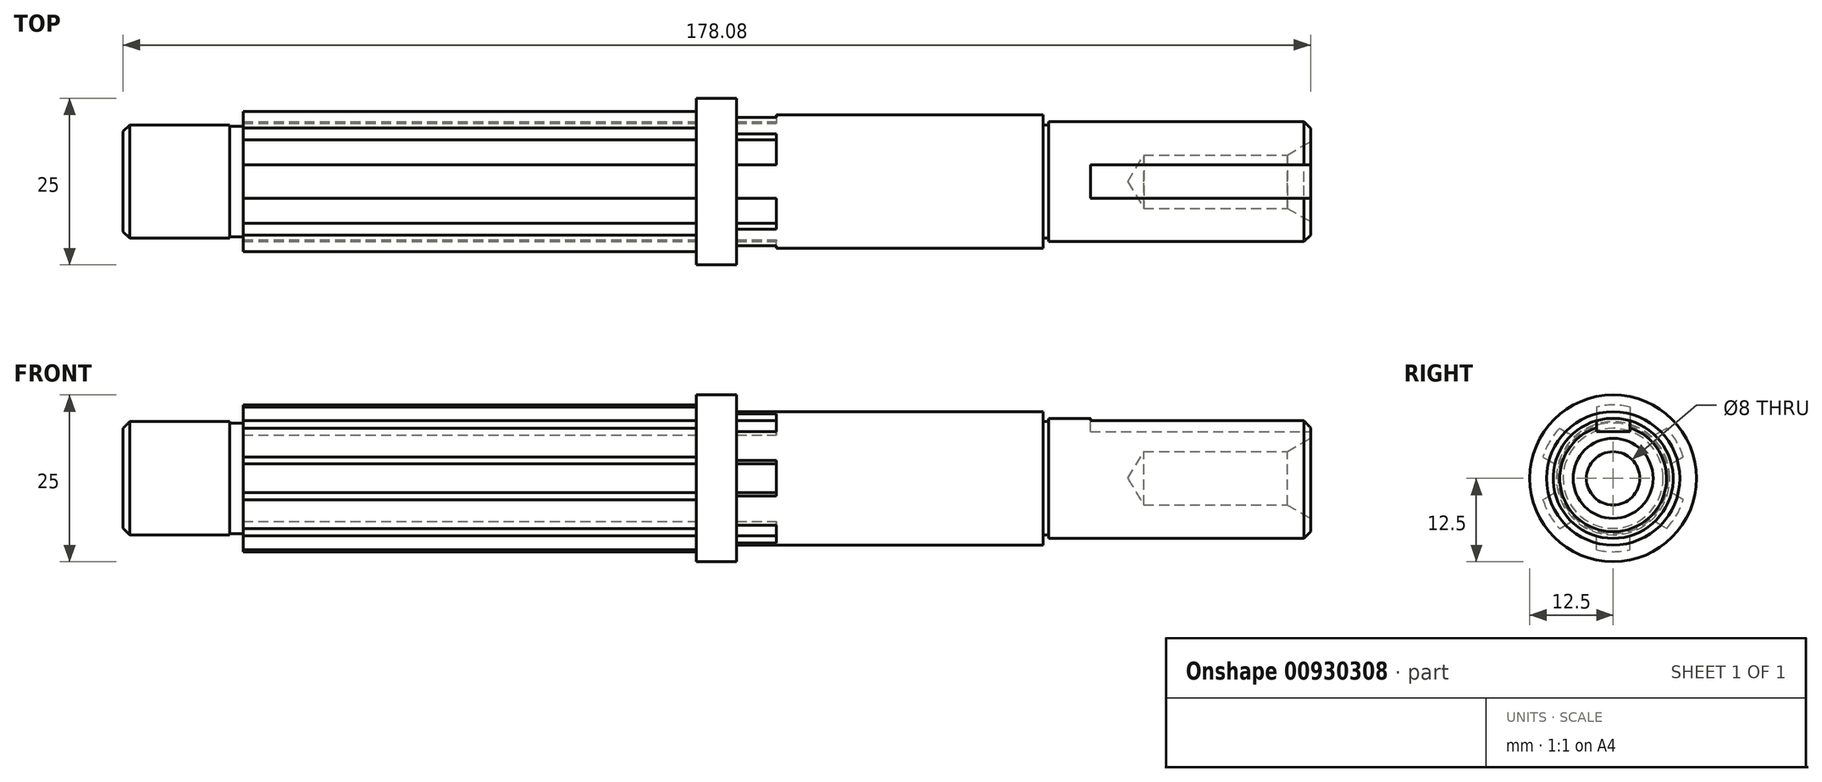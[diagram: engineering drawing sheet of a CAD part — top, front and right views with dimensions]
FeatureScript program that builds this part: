
annotation { "Feature Type Name" : "Feature", "Feature Type Description" : "" }
export const myFeature = defineFeature(function(context is Context, id is Id, definition is map)
    precondition{}
    {
        {
            var Q0;
            Q0=qCreatedBy(makeId("Front.planeOp"),FACE);
            var sketch = newSketch(context, id + "F0", { "sketchPlane" : qUnion([Q0])});
            skLineSegment(sketch, "E0", {"start": v(0, 0) * mm, "end": v(0, 10) * mm});
            skLineSegment(sketch, "E1", {"start": v(0, 10) * mm, "end": v(46, 10) * mm});
            skLineSegment(sketch, "E2", {"start": v(46, 10) * mm, "end": v(46, 8.5) * mm});
            skLineSegment(sketch, "E3", {"start": v(46, 8.5) * mm, "end": v(52.78, 8.5) * mm});
            skLineSegment(sketch, "E4", {"start": v(52.78, 8.5) * mm, "end": v(52.78, 9) * mm});
            skLineSegment(sketch, "E5", {"start": v(52.78, 9) * mm, "end": v(85.08, 9) * mm});
            skLineSegment(sketch, "E6", {"start": v(85.08, 9) * mm, "end": v(86.08, 8) * mm});
            skLineSegment(sketch, "E7", {"start": v(86.08, 8) * mm, "end": v(86.08, 0) * mm});
            skLineSegment(sketch, "E8", {"start": v(86.08, 0) * mm, "end": v(0, 0) * mm});
            skSolve(sketch);
        }
        {
            var Q0;
            Q0=makeQuery(id+"F0.imprint","IMPRINT",FACE,{"disambiguationData":[TD([[makeQuery(id+"F0.imprint","IMPRINT",EDGE,{"derivedFrom":sQuery(id+"F0.wireOp",EDGE,"E0")}),-1.0]])]});
            var Q1;
            Q1=sQuery(id+"F0.wireOp",EDGE,"E8");
            revolve(context, id + "F1", {"surfaceOperationType" : NewSurfaceOperationType.NEW, "entities" : qUnion([Q0]), "axis" : qUnion([Q1]), "revolveType" : RevolveType.FULL});
        }
        {
            var Q0;
            Q0=makeQuery(id+"F1.opRevolve","SWEPT_FACE",FACE,{"disambiguationData":[OSD([sQuery(id+"F0.wireOp",EDGE,"E0")])]});
            var sketch = newSketch(context, id + "F2", { "sketchPlane" : qUnion([Q0])});
            skCircle(sketch, "E9", {"center": v(0, 0) * mm, "radius": 12.5 * mm});
            skSolve(sketch);
        }
        {
            var Q0;
            Q0 = qSketchRegion(id + "F2", true);
            extrude(context, id + "F3", {"entities" : qUnion([Q0]), "operationType" : NewBodyOperationType.ADD, "depth" : 6 * mm, "offsetDistance" : 25 * mm});
        }
        {
            var Q0;
            Q0=makeQuery(id+"F3.opExtrude","CAP_FACE",FACE,{"disambiguationData":[OSD([sQuery(id+"F2.wireOp",EDGE,"E9")])],"isStart":false});
            var sketch = newSketch(context, id + "F4", { "sketchPlane" : qUnion([Q0])});
            skArc(sketch, "E10", {"start": v(6.24, 6.49) * mm, "mid": v(4.5, 7.8) * mm, "end": v(2.5, 8.65) * mm});
            skArc(sketch, "E11", {"start": v(10.53, 3.2) * mm, "mid": v(9.53, 5.5) * mm, "end": v(8.03, 7.52) * mm});
            skLineSegment(sketch, "E12", {"start": v(0, 0) * mm, "end": v(9.53, 5.5) * mm});
            skLineSegment(sketch, "E13", {"start": v(8.03, 7.52) * mm, "end": v(6.24, 6.49) * mm});
            skLineSegment(sketch, "E14", {"start": v(10.53, 3.2) * mm, "end": v(8.74, 2.16) * mm});
            skPoint(sketch, "E15.orphan", {"position": v(8.28, 7.67) * mm});
            skPoint(sketch, "E16.MirrorCS.start.orphan", {"position": v(9.53, 5.5) * mm});
            skPoint(sketch, "E17.orphan", {"position": v(10.78, 3.33) * mm});
            skArc(sketch, "E18.1.0", {"start": v(2.5, 10.71) * mm, "mid": v(0, 11) * mm, "end": v(-2.5, 10.71) * mm});
            skLineSegment(sketch, "E18.1.1", {"start": v(2.5, 10.71) * mm, "end": v(2.5, 8.65) * mm});
            skLineSegment(sketch, "E18.1.2", {"start": v(-2.5, 10.71) * mm, "end": v(-2.5, 8.65) * mm});
            skArc(sketch, "E18.2.0", {"start": v(-8.03, 7.52) * mm, "mid": v(-9.53, 5.5) * mm, "end": v(-10.53, 3.2) * mm});
            skLineSegment(sketch, "E18.2.1", {"start": v(-8.03, 7.52) * mm, "end": v(-6.24, 6.49) * mm});
            skLineSegment(sketch, "E18.2.2", {"start": v(-10.53, 3.2) * mm, "end": v(-8.74, 2.16) * mm});
            skArc(sketch, "E18.3.0", {"start": v(-10.53, -3.2) * mm, "mid": v(-9.53, -5.5) * mm, "end": v(-8.03, -7.52) * mm});
            skLineSegment(sketch, "E18.3.1", {"start": v(-10.53, -3.2) * mm, "end": v(-8.74, -2.16) * mm});
            skLineSegment(sketch, "E18.3.2", {"start": v(-8.03, -7.52) * mm, "end": v(-6.24, -6.49) * mm});
            skArc(sketch, "E18.4.0", {"start": v(-2.5, -10.71) * mm, "mid": v(0, -11) * mm, "end": v(2.5, -10.71) * mm});
            skLineSegment(sketch, "E18.4.1", {"start": v(-2.5, -10.71) * mm, "end": v(-2.5, -8.65) * mm});
            skLineSegment(sketch, "E18.4.2", {"start": v(2.5, -10.71) * mm, "end": v(2.5, -8.65) * mm});
            skArc(sketch, "E18.5.0", {"start": v(8.03, -7.52) * mm, "mid": v(9.53, -5.5) * mm, "end": v(10.53, -3.2) * mm});
            skLineSegment(sketch, "E18.5.1", {"start": v(8.03, -7.52) * mm, "end": v(6.24, -6.49) * mm});
            skLineSegment(sketch, "E18.5.2", {"start": v(10.53, -3.2) * mm, "end": v(8.74, -2.16) * mm});
            skArc(sketch, "E19.trimOffspring", {"start": v(-2.5, 8.65) * mm, "mid": v(-4.5, 7.8) * mm, "end": v(-6.24, 6.49) * mm});
            skArc(sketch, "E20.trimOffspring", {"start": v(-8.74, 2.16) * mm, "mid": v(-9, 0) * mm, "end": v(-8.74, -2.16) * mm});
            skArc(sketch, "E21.trimOffspring", {"start": v(-6.24, -6.49) * mm, "mid": v(-4.5, -7.8) * mm, "end": v(-2.5, -8.65) * mm});
            skArc(sketch, "E22.trimOffspring", {"start": v(2.5, -8.65) * mm, "mid": v(4.5, -7.8) * mm, "end": v(6.24, -6.49) * mm});
            skArc(sketch, "E23.trimOffspring", {"start": v(8.74, -2.16) * mm, "mid": v(9, 0) * mm, "end": v(8.74, 2.16) * mm});
            skSolve(sketch);
        }
        {
            var Q0;
            Q0 = qSketchRegion(id + "F4", true);
            extrude(context, id + "F5", {"entities" : qUnion([Q0]), "operationType" : NewBodyOperationType.ADD, "depth" : 68 * mm, "offsetDistance" : 25 * mm});
        }
        {
            var Q0;
            Q0=makeQuery(id+"F3.opExtrude","CAP_FACE",FACE,{"disambiguationData":[OSD([sQuery(id+"F2.wireOp",EDGE,"E9")])],"isStart":false});
            var sketch = newSketch(context, id + "F6", { "sketchPlane" : qUnion([Q0])});
            skCircle(sketch, "E24.0.0", {"center": v(0, 0) * mm, "radius": 12.5 * mm});
            skArc(sketch, "E25.0", {"start": v(6.24, 6.49) * mm, "mid": v(4.5, 7.8) * mm, "end": v(2.5, 8.65) * mm});
            skLineSegment(sketch, "E26.0", {"start": v(2.5, 10.71) * mm, "end": v(2.5, 8.65) * mm});
            skArc(sketch, "E27.0", {"start": v(2.5, 10.71) * mm, "mid": v(0, 11) * mm, "end": v(-2.5, 10.71) * mm});
            skLineSegment(sketch, "E28.0", {"start": v(-2.5, 10.71) * mm, "end": v(-2.5, 8.65) * mm});
            skArc(sketch, "E29.0", {"start": v(-2.5, 8.65) * mm, "mid": v(-4.5, 7.8) * mm, "end": v(-6.24, 6.49) * mm});
            skLineSegment(sketch, "E30.0", {"start": v(-8.03, 7.52) * mm, "end": v(-6.24, 6.49) * mm});
            skArc(sketch, "E31.0", {"start": v(-8.03, 7.52) * mm, "mid": v(-9.53, 5.5) * mm, "end": v(-10.53, 3.2) * mm});
            skLineSegment(sketch, "E32.0", {"start": v(-10.53, 3.2) * mm, "end": v(-8.74, 2.16) * mm});
            skArc(sketch, "E33.0", {"start": v(-8.74, 2.16) * mm, "mid": v(-9, 0) * mm, "end": v(-8.74, -2.16) * mm});
            skLineSegment(sketch, "E34.0", {"start": v(-10.53, -3.2) * mm, "end": v(-8.74, -2.16) * mm});
            skArc(sketch, "E35.0", {"start": v(-10.53, -3.2) * mm, "mid": v(-9.53, -5.5) * mm, "end": v(-8.03, -7.52) * mm});
            skLineSegment(sketch, "E36.0", {"start": v(-8.03, -7.52) * mm, "end": v(-6.24, -6.49) * mm});
            skArc(sketch, "E37.0", {"start": v(-6.24, -6.49) * mm, "mid": v(-4.5, -7.8) * mm, "end": v(-2.5, -8.65) * mm});
            skLineSegment(sketch, "E38.0", {"start": v(-2.5, -10.71) * mm, "end": v(-2.5, -8.65) * mm});
            skArc(sketch, "E39.0", {"start": v(-2.5, -10.71) * mm, "mid": v(0, -11) * mm, "end": v(2.5, -10.71) * mm});
            skLineSegment(sketch, "E40.0", {"start": v(2.5, -10.71) * mm, "end": v(2.5, -8.65) * mm});
            skArc(sketch, "E41.0", {"start": v(2.5, -8.65) * mm, "mid": v(4.5, -7.8) * mm, "end": v(6.24, -6.49) * mm});
            skLineSegment(sketch, "E42.0", {"start": v(8.03, -7.52) * mm, "end": v(6.24, -6.49) * mm});
            skArc(sketch, "E43.0", {"start": v(8.03, -7.52) * mm, "mid": v(9.53, -5.5) * mm, "end": v(10.53, -3.2) * mm});
            skLineSegment(sketch, "E44.0", {"start": v(10.53, -3.2) * mm, "end": v(8.74, -2.16) * mm});
            skArc(sketch, "E45.0", {"start": v(8.74, -2.16) * mm, "mid": v(9, 0) * mm, "end": v(8.74, 2.16) * mm});
            skLineSegment(sketch, "E46.0", {"start": v(10.53, 3.2) * mm, "end": v(8.74, 2.16) * mm});
            skArc(sketch, "E47.0", {"start": v(10.53, 3.2) * mm, "mid": v(9.53, 5.5) * mm, "end": v(8.03, 7.52) * mm});
            skLineSegment(sketch, "E48.0", {"start": v(8.03, 7.52) * mm, "end": v(6.24, 6.49) * mm});
            skSolve(sketch);
        }
        {
            var Q0;
            Q0 = qSketchRegion(id + "F6", true);
            extrude(context, id + "F7", {"entities" : qUnion([Q0]), "operationType" : NewBodyOperationType.REMOVE, "oppositeDirection" : true, "depth" : 12 * mm, "offsetDistance" : 25 * mm});
        }
        {
            var Q0;
            Q0 = qSketchRegion(id + "F6", true);
            extrude(context, id + "F8", {"entities" : qUnion([Q0]), "operationType" : NewBodyOperationType.ADD, "oppositeDirection" : true, "depth" : 6 * mm, "offsetDistance" : 25 * mm});
        }
        {
            var Q0;
            Q0=qCreatedBy(makeId("Front.planeOp"),FACE);
            var sketch = newSketch(context, id + "F9", { "sketchPlane" : qUnion([Q0])});
            skLineSegment(sketch, "E49.0", {"start": v(-74, -2.16) * mm, "end": v(-74, 2.16) * mm});
            skLineSegment(sketch, "E50.0", {"start": v(-74, 3.2) * mm, "end": v(-74, 7.52) * mm});
            skLineSegment(sketch, "E51.0", {"start": v(-74, -7.52) * mm, "end": v(-74, -3.2) * mm});
            skLineSegment(sketch, "E52.0.0", {"start": v(-74, -2.16) * mm, "end": v(-6, -2.16) * mm});
            skLineSegment(sketch, "E52.0.1", {"start": v(-6, -2.16) * mm, "end": v(-6, 2.16) * mm});
            skLineSegment(sketch, "E52.0.3", {"start": v(-74, 2.16) * mm, "end": v(-74, -2.16) * mm});
            skLineSegment(sketch, "E53", {"start": v(-74, 8.3) * mm, "end": v(-76, 8.3) * mm});
            skLineSegment(sketch, "E54", {"start": v(-76, 8.3) * mm, "end": v(-76, 8.5) * mm});
            skLineSegment(sketch, "E55", {"start": v(-76, 8.5) * mm, "end": v(-91, 8.5) * mm});
            skLineSegment(sketch, "E56", {"start": v(-91, 8.5) * mm, "end": v(-92, 7.5) * mm});
            skLineSegment(sketch, "E57", {"start": v(-92, 7.5) * mm, "end": v(-92, 0) * mm});
            skPoint(sketch, "E57.endSnap0", {"position": v(-74, 0) * mm});
            skLineSegment(sketch, "E58", {"start": v(-92, 0) * mm, "end": v(-74, 0) * mm});
            skLineSegment(sketch, "E59", {"start": v(-74, 0) * mm, "end": v(-74, 8.3) * mm});
            skSolve(sketch);
        }
        {
            var Q0;
            {var subQ0=sQuery(id+"F9.wireOp",EDGE,"E53");Q0=makeQuery(id+"F9.imprint","IMPRINT",FACE,{"disambiguationData":[TD([[makeQuery(id+"F9.imprint","IMPRINT",EDGE,{"derivedFrom":subQ0}),1.0]])]});}
            var Q1;
            Q1=sQuery(id+"F9.wireOp",EDGE,"E58");
            revolve(context, id + "F10", {"operationType" : NewBodyOperationType.ADD, "surfaceOperationType" : NewSurfaceOperationType.NEW, "entities" : qUnion([Q0]), "axis" : qUnion([Q1]), "revolveType" : RevolveType.FULL});
        }
        {
            var Q0;
            Q0=makeQuery(id+"F1.opRevolve","SWEPT_FACE",FACE,{"disambiguationData":[OSD([sQuery(id+"F0.wireOp",EDGE,"E7")])]});
            var sketch = newSketch(context, id + "F11", { "sketchPlane" : qUnion([Q0])});
            skPoint(sketch, "E60", {"position": v(0, 0) * mm});
            skSolve(sketch);
        }
        {
            var Q0;
            Q0=sQuery(id+"F11.wireOp",VERTEX,"E60");
            var Q1;
            Q1=makeQuery(id+"F1.opRevolve","SWEPT_BODY",BODY,{"disambiguationData":[OSD([sQuery(id+"F0.wireOp",EDGE,"E0"),sQuery(id+"F0.wireOp",EDGE,"E1"),sQuery(id+"F0.wireOp",EDGE,"E2"),sQuery(id+"F0.wireOp",EDGE,"E3"),sQuery(id+"F0.wireOp",EDGE,"E4"),sQuery(id+"F0.wireOp",EDGE,"E5"),sQuery(id+"F0.wireOp",EDGE,"E6"),sQuery(id+"F0.wireOp",EDGE,"E7"),sQuery(id+"F0.wireOp",EDGE,"E8")])]});
            hole(context, id + "F12", {"style" : HoleStyle.C_SINK, "endStyle" : HoleEndStyle.BLIND, "holeDiameter" : 8 * mm, "cSinkDiameter" : 12 * mm, "cSinkAngle" : 60 * degree, "majorDiameter" : 5 * mm, "holeDepth" : 25 * mm, "isTappedThrough" : true, "tappedDepth" : 12 * mm, "tapClearance" : 3, "locations" : qUnion([Q0]), "scope" : qUnion([Q1])});
        }
        {
            var Q0;
            Q0=makeQuery(id+"F1.opRevolve","SWEPT_FACE",FACE,{"disambiguationData":[OSD([sQuery(id+"F0.wireOp",EDGE,"E7")])]});
            var sketch = newSketch(context, id + "F13", { "sketchPlane" : qUnion([Q0])});
            skLineSegment(sketch, "E61", {"start": v(0, 7) * mm, "end": v(-2.5, 7) * mm});
            skLineSegment(sketch, "E62.MirrorCS", {"start": v(0, 7) * mm, "end": v(2.5, 7) * mm});
            skArc(sketch, "E63.0", {"start": v(2.5, 8.65) * mm, "mid": v(0, 9) * mm, "end": v(-2.5, 8.65) * mm});
            skLineSegment(sketch, "E64", {"start": v(-2.5, 7) * mm, "end": v(-2.5, 8.65) * mm});
            skLineSegment(sketch, "E65", {"start": v(2.5, 7) * mm, "end": v(2.5, 8.65) * mm});
            skPoint(sketch, "E66.end.orphan", {"position": v(0, -9) * mm});
            skSolve(sketch);
        }
        {
            var Q0;
            Q0 = qSketchRegion(id + "F13", true);
            extrude(context, id + "F14", {"entities" : qUnion([Q0]), "operationType" : NewBodyOperationType.REMOVE, "oppositeDirection" : true, "depth" : 33 * mm, "offsetDistance" : 25 * mm});
        }
        {
            var Q0;
            Q0=makeQuery(id+"F1.opRevolve","SWEPT_FACE",FACE,{"disambiguationData":[OSD([sQuery(id+"F0.wireOp",EDGE,"E4")])]});
            var sketch = newSketch(context, id + "F15", { "sketchPlane" : qUnion([Q0])});
            skSolve(sketch);
        }
        {
            var Q0;
            Q0 = qSketchRegion(id + "F15", true);
            var Q1;
            {var subQ0=sQuery(id+"F0.wireOp",EDGE,"E4");Q1=makeQuery(id+"F15.imprint","IMPRINT",FACE,{"disambiguationData":[TD([[makeQuery(id+"F15.imprint","IMPRINT",EDGE,{"derivedFrom":makeQuery(id+"F1.opRevolve","SWEPT_EDGE",EDGE,{"disambiguationData":[OSD([sQuery(id+"F0.wireOp",EDGE,"E3"),subQ0])]})}),1.0]])]});}
            extrude(context, id + "F16", {"entities" : qUnion([Q0, Q1]), "operationType" : NewBodyOperationType.ADD, "depth" : 6 * mm, "offsetDistance" : 25 * mm});
        }
    });
